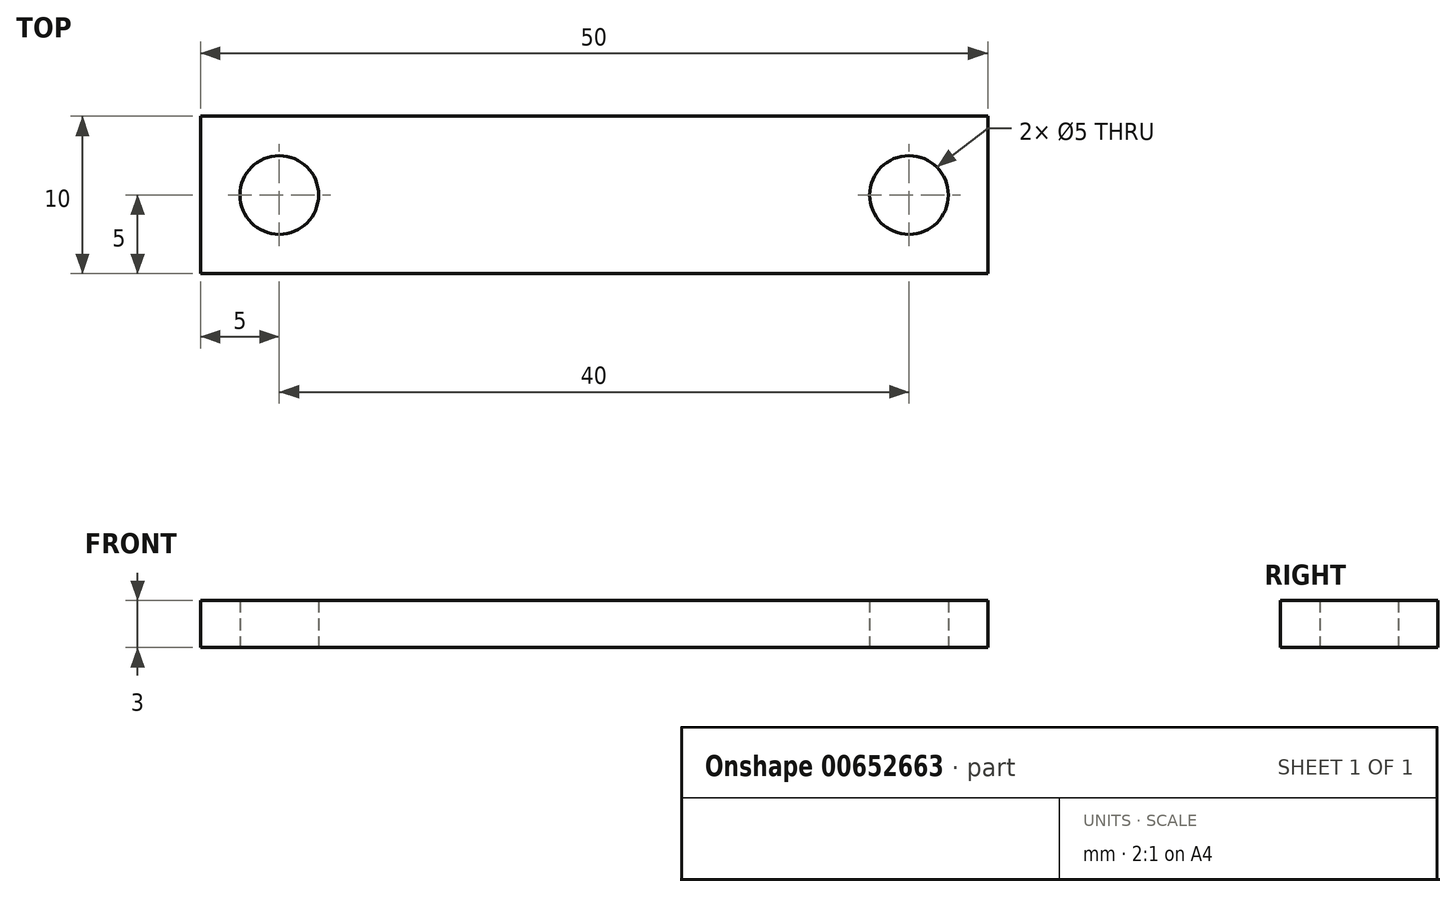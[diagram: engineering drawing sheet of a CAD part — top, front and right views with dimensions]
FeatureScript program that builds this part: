
annotation { "Feature Type Name" : "Feature", "Feature Type Description" : "" }
export const myFeature = defineFeature(function(context is Context, id is Id, definition is map)
    precondition{}
    {
        {
            var Q0;
            Q0=qCreatedBy(makeId("Top.planeOp"),FACE);
            var sketch = newSketch(context, id + "F0", { "sketchPlane" : qUnion([Q0])});
            skLineSegment(sketch, "E0.bottom", {"start": v(25, -5) * mm, "end": v(-25, -5) * mm});
            skLineSegment(sketch, "E0.top", {"start": v(25, 5) * mm, "end": v(-25, 5) * mm});
            skLineSegment(sketch, "E0.left", {"start": v(25, -5) * mm, "end": v(25, 5) * mm});
            skLineSegment(sketch, "E0.right", {"start": v(-25, -5) * mm, "end": v(-25, 5) * mm});
            skPoint(sketch, "E0.middle", {"position": v(0, 0) * mm});
            skCircle(sketch, "E1", {"center": v(-20, 0) * mm, "radius": 2.5 * mm});
            skPoint(sketch, "E1.centerSnap0", {"position": v(-25, 0) * mm});
            skCircle(sketch, "E2", {"center": v(20, 0) * mm, "radius": 2.5 * mm});
            skLineSegment(sketch, "E3", {"start": v(-25, 0) * mm, "end": v(-20, 0) * mm, "construction": true});
            skLineSegment(sketch, "E4", {"start": v(-20, 5) * mm, "end": v(-20, 0) * mm, "construction": true});
            skLineSegment(sketch, "E5", {"start": v(20, 5) * mm, "end": v(20, 0) * mm, "construction": true});
            skLineSegment(sketch, "E6", {"start": v(25, 0) * mm, "end": v(20, 0) * mm, "construction": true});
            skSolve(sketch);
        }
        {
            var Q0;
            Q0=makeQuery(id+"F0.imprint","IMPRINT",FACE,{"disambiguationData":[TD([[makeQuery(id+"F0.imprint","IMPRINT",EDGE,{"derivedFrom":sQuery(id+"F0.wireOp",EDGE,"E0.bottom")}),-1.0]])]});
            extrude(context, id + "F1", {"entities" : qUnion([Q0]), "depth" : 3 * mm, "offsetDistance" : 25 * mm});
        }
    });
